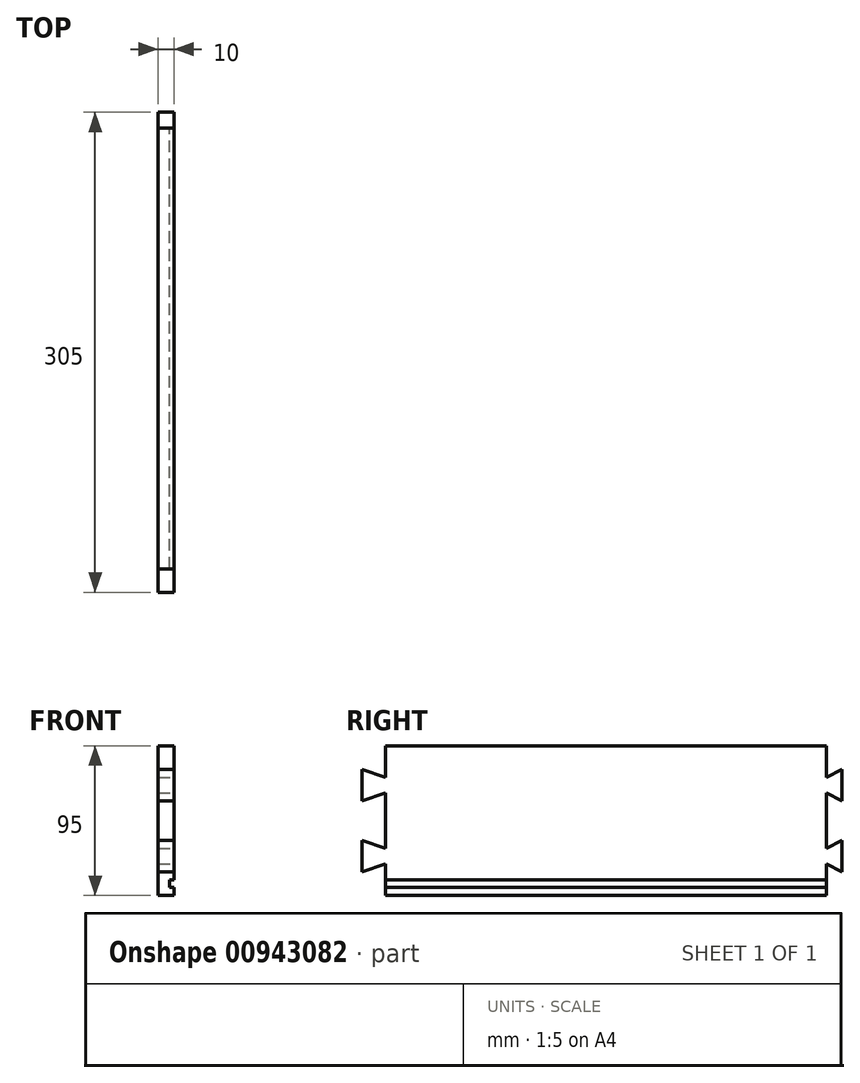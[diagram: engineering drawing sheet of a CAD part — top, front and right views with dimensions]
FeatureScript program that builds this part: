
annotation { "Feature Type Name" : "Feature", "Feature Type Description" : "" }
export const myFeature = defineFeature(function(context is Context, id is Id, definition is map)
    precondition{}
    {
        {
            var Q0;
            Q0=qCreatedBy(makeId("Right.planeOp"),FACE);
            var sketch = newSketch(context, id + "F0", { "sketchPlane" : qUnion([Q0])});
            skLineSegment(sketch, "E0.bottom", {"start": v(-82.46, 55.9) * mm, "end": v(222.54, 55.9) * mm});
            skLineSegment(sketch, "E0.top", {"start": v(-82.46, -39.1) * mm, "end": v(222.54, -39.1) * mm});
            skLineSegment(sketch, "E0.left", {"start": v(-82.46, 55.9) * mm, "end": v(-82.46, -39.1) * mm});
            skLineSegment(sketch, "E0.right", {"start": v(222.54, 55.9) * mm, "end": v(222.54, -39.1) * mm});
            skSolve(sketch);
        }
        {
            var Q0;
            Q0=makeQuery(id+"F0.imprint","IMPRINT",FACE,{"disambiguationData":[TD([[makeQuery(id+"F0.imprint","IMPRINT",EDGE,{"derivedFrom":sQuery(id+"F0.wireOp",EDGE,"E0.bottom")}),-1.0]])]});
            extrude(context, id + "F1", {"entities" : qUnion([Q0]), "depth" : 10 * mm, "offsetDistance" : 25 * mm});
        }
        {
            var Q0;
            Q0=makeQuery(id+"F1.opExtrude","CAP_FACE",FACE,{"disambiguationData":[OSD([sQuery(id+"F0.wireOp",EDGE,"E0.bottom"),sQuery(id+"F0.wireOp",EDGE,"E0.top"),sQuery(id+"F0.wireOp",EDGE,"E0.left"),sQuery(id+"F0.wireOp",EDGE,"E0.right")])],"isStart":false});
            var sketch = newSketch(context, id + "F2", { "sketchPlane" : qUnion([Q0])});
            skLineSegment(sketch, "E1", {"start": v(-82.46, 40.9) * mm, "end": v(-67.46, 35.9) * mm});
            skLineSegment(sketch, "E2", {"start": v(-67.46, 35.9) * mm, "end": v(-67.46, 55.9) * mm});
            skLineSegment(sketch, "E3", {"start": v(-67.46, 55.9) * mm, "end": v(-82.46, 55.9) * mm});
            skLineSegment(sketch, "E4", {"start": v(-82.46, 55.9) * mm, "end": v(-82.46, 40.9) * mm});
            skLineSegment(sketch, "E5", {"start": v(-82.46, -39.1) * mm, "end": v(-82.46, -24.1) * mm});
            skLineSegment(sketch, "E6", {"start": v(-82.46, -24.1) * mm, "end": v(-67.46, -19.1) * mm});
            skLineSegment(sketch, "E7", {"start": v(-67.46, -19.1) * mm, "end": v(-67.46, -39.1) * mm});
            skLineSegment(sketch, "E8", {"start": v(-67.46, -39.1) * mm, "end": v(-82.46, -39.1) * mm});
            skLineSegment(sketch, "E9", {"start": v(-82.46, 20.9) * mm, "end": v(-67.46, 25.9) * mm});
            skLineSegment(sketch, "E10", {"start": v(-67.46, 25.9) * mm, "end": v(-67.46, -9.1) * mm});
            skLineSegment(sketch, "E11", {"start": v(-67.46, -9.1) * mm, "end": v(-82.46, -4.1) * mm});
            skSolve(sketch);
        }
        {
            var Q0;
            Q0=makeQuery(id+"F2.imprint","IMPRINT",FACE,{"disambiguationData":[TD([[makeQuery(id+"F2.imprint","IMPRINT",EDGE,{"derivedFrom":sQuery(id+"F2.wireOp",EDGE,"E1")}),1.0]])]});
            var Q1;
            {var subQ0=sQuery(id+"F2.wireOp",EDGE,"E9");Q1=makeQuery(id+"F2.imprint","IMPRINT",FACE,{"disambiguationData":[TD([[makeQuery(id+"F2.imprint","IMPRINT",EDGE,{"derivedFrom":subQ0}),-1.0]])]});}
            var Q2;
            Q2=makeQuery(id+"F2.imprint","IMPRINT",FACE,{"disambiguationData":[TD([[makeQuery(id+"F2.imprint","IMPRINT",EDGE,{"derivedFrom":sQuery(id+"F2.wireOp",EDGE,"E5")}),1.0]])]});
            extrude(context, id + "F3", {"entities" : qUnion([Q0, Q1, Q2]), "operationType" : NewBodyOperationType.REMOVE, "oppositeDirection" : true, "depth" : 25 * mm, "offsetDistance" : 25 * mm});
        }
        {
            var Q0;
            Q0=makeQuery(id+"F1.opExtrude","CAP_FACE",FACE,{"disambiguationData":[OSD([sQuery(id+"F0.wireOp",EDGE,"E0.bottom"),sQuery(id+"F0.wireOp",EDGE,"E0.top"),sQuery(id+"F0.wireOp",EDGE,"E0.left"),sQuery(id+"F0.wireOp",EDGE,"E0.right")])],"isStart":false});
            var sketch = newSketch(context, id + "F4", { "sketchPlane" : qUnion([Q0])});
            skLineSegment(sketch, "E12.bottom", {"start": v(-67.46, -34.1) * mm, "end": v(222.54, -34.1) * mm});
            skLineSegment(sketch, "E12.top", {"start": v(-67.46, -29.1) * mm, "end": v(222.54, -29.1) * mm});
            skLineSegment(sketch, "E12.left", {"start": v(-67.46, -34.1) * mm, "end": v(-67.46, -29.1) * mm});
            skLineSegment(sketch, "E12.right", {"start": v(222.54, -34.1) * mm, "end": v(222.54, -29.1) * mm});
            skSolve(sketch);
        }
        {
            var Q0;
            Q0=makeQuery(id+"F4.imprint","IMPRINT",FACE,{"disambiguationData":[TD([[makeQuery(id+"F4.imprint","IMPRINT",EDGE,{"derivedFrom":sQuery(id+"F4.wireOp",EDGE,"E12.bottom")}),1.0]])]});
            extrude(context, id + "F5", {"entities" : qUnion([Q0]), "operationType" : NewBodyOperationType.REMOVE, "oppositeDirection" : true, "depth" : 3 * mm, "offsetDistance" : 25 * mm});
        }
        {
            var Q0;
            Q0=makeQuery(id+"F1.opExtrude","CAP_FACE",FACE,{"disambiguationData":[OSD([sQuery(id+"F0.wireOp",EDGE,"E0.bottom"),sQuery(id+"F0.wireOp",EDGE,"E0.top"),sQuery(id+"F0.wireOp",EDGE,"E0.left"),sQuery(id+"F0.wireOp",EDGE,"E0.right")])],"isStart":true});
            var sketch = newSketch(context, id + "F6", { "sketchPlane" : qUnion([Q0])});
            skLineSegment(sketch, "E13", {"start": v(-222.54, 55.9) * mm, "end": v(-222.54, 40.9) * mm});
            skLineSegment(sketch, "E14", {"start": v(-222.54, 40.9) * mm, "end": v(-212.54, 35.9) * mm});
            skLineSegment(sketch, "E15", {"start": v(-212.54, 35.9) * mm, "end": v(-212.54, 55.9) * mm});
            skLineSegment(sketch, "E16", {"start": v(-222.54, 20.9) * mm, "end": v(-212.54, 25.9) * mm});
            skLineSegment(sketch, "E17", {"start": v(-212.54, 25.9) * mm, "end": v(-212.54, -9.1) * mm});
            skLineSegment(sketch, "E18", {"start": v(-212.54, -9.1) * mm, "end": v(-222.54, -4.1) * mm});
            skLineSegment(sketch, "E19", {"start": v(-222.54, -24.1) * mm, "end": v(-212.54, -19.1) * mm});
            skLineSegment(sketch, "E20", {"start": v(-212.54, -19.1) * mm, "end": v(-212.54, -39.1) * mm});
            skLineSegment(sketch, "E21", {"start": v(-212.54, -39.1) * mm, "end": v(-222.54, -39.1) * mm});
            skLineSegment(sketch, "E22", {"start": v(-222.54, -39.1) * mm, "end": v(-222.54, -24.1) * mm});
            skSolve(sketch);
        }
        {
            var Q0;
            {var subQ0=sQuery(id+"F6.wireOp",EDGE,"E16");Q0=makeQuery(id+"F6.imprint","IMPRINT",FACE,{"disambiguationData":[TD([[makeQuery(id+"F6.imprint","IMPRINT",EDGE,{"derivedFrom":subQ0}),-1.0]])]});}
            var Q1;
            Q1=makeQuery(id+"F6.imprint","IMPRINT",FACE,{"disambiguationData":[TD([[makeQuery(id+"F6.imprint","IMPRINT",EDGE,{"derivedFrom":sQuery(id+"F6.wireOp",EDGE,"E19")}),-1.0]])]});
            var Q2;
            {var subQ0=sQuery(id+"F6.wireOp",EDGE,"E13");Q2=makeQuery(id+"F6.imprint","IMPRINT",FACE,{"disambiguationData":[TD([[makeQuery(id+"F6.imprint","IMPRINT",EDGE,{"derivedFrom":subQ0}),1.0]])]});}
            extrude(context, id + "F7", {"entities" : qUnion([Q0, Q1, Q2]), "operationType" : NewBodyOperationType.REMOVE, "oppositeDirection" : true, "depth" : 25 * mm, "offsetDistance" : 25 * mm});
        }
    });
